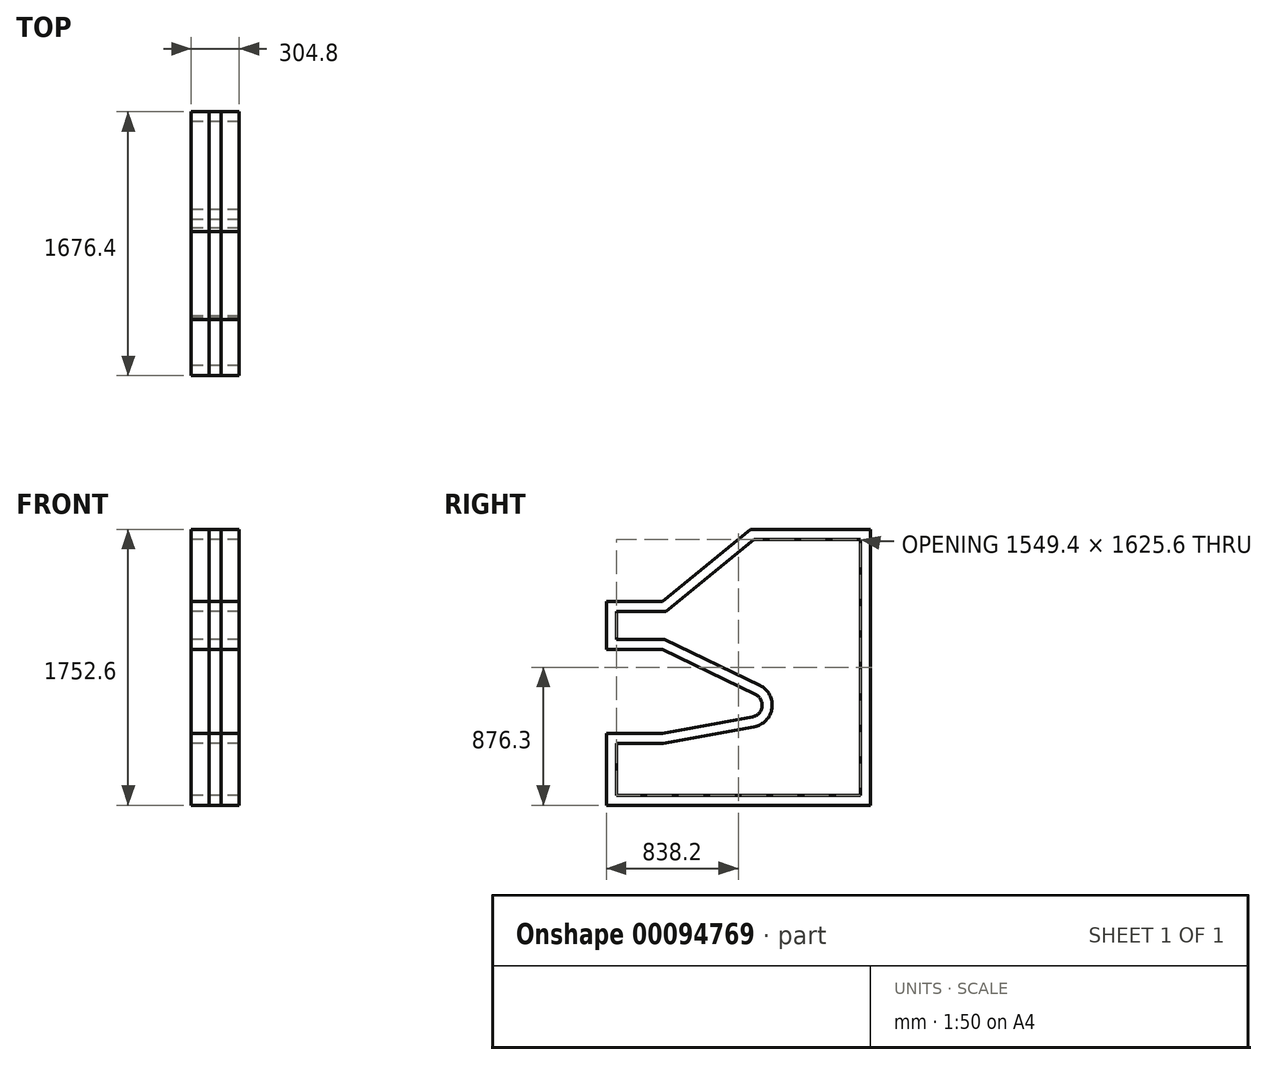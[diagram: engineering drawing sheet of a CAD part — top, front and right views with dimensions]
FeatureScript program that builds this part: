
annotation { "Feature Type Name" : "Feature", "Feature Type Description" : "" }
export const myFeature = defineFeature(function(context is Context, id is Id, definition is map)
    precondition{}
    {
        {
            var Q0;
            Q0=qCreatedBy(makeId("Right.planeOp"),FACE);
            var sketch = newSketch(context, id + "F0", { "sketchPlane" : qUnion([Q0])});
            skLineSegment(sketch, "E0", {"start": v(-914.4, 0) * mm, "end": v(762, 0) * mm, "construction": true});
            skLineSegment(sketch, "E1.0", {"start": v(-914.4, 457.2) * mm, "end": v(0, 457.2) * mm, "construction": true});
            skLineSegment(sketch, "E2.0", {"start": v(-1354.22, 635) * mm, "end": v(1358.95, 635) * mm, "construction": true});
            skLineSegment(sketch, "E3.0", {"start": v(-914.4, 990.6) * mm, "end": v(0, 990.6) * mm, "construction": true});
            skLineSegment(sketch, "E4.0", {"start": v(-914.4, 1295.4) * mm, "end": v(0, 1295.4) * mm, "construction": true});
            skLineSegment(sketch, "E5", {"start": v(-914.4, 1295.4) * mm, "end": v(-914.4, 0) * mm, "construction": true});
            skLineSegment(sketch, "E6.0", {"start": v(-558.8, 1295.4) * mm, "end": v(-558.8, 0) * mm, "construction": true});
            skLineSegment(sketch, "E7.0", {"start": v(-1354.22, 1752.6) * mm, "end": v(1358.95, 1752.6) * mm, "construction": true});
            skLineSegment(sketch, "E8", {"start": v(0, -258.78) * mm, "end": v(0, 1895.33) * mm, "construction": true});
            skLineSegment(sketch, "E9.0", {"start": v(762, -258.78) * mm, "end": v(762, 1895.33) * mm, "construction": true});
            skArc(sketch, "E10", {"start": v(13.47, 560) * mm, "mid": v(75.49, 624.6) * mm, "end": v(33.24, 703.57) * mm});
            skLineSegment(sketch, "E11", {"start": v(-558.8, 990.6) * mm, "end": v(33.24, 703.57) * mm});
            skLineSegment(sketch, "E12", {"start": v(-558.8, 457.2) * mm, "end": v(13.47, 560) * mm});
            skLineSegment(sketch, "E13", {"start": v(-558.8, 990.6) * mm, "end": v(-914.4, 990.6) * mm});
            skLineSegment(sketch, "E14", {"start": v(-914.4, 990.6) * mm, "end": v(-914.4, 1295.4) * mm});
            skLineSegment(sketch, "E15", {"start": v(-914.4, 1295.4) * mm, "end": v(-558.8, 1295.4) * mm});
            skLineSegment(sketch, "E16", {"start": v(-558.8, 1295.4) * mm, "end": v(0, 1752.6) * mm});
            skLineSegment(sketch, "E17", {"start": v(0, 1752.6) * mm, "end": v(762, 1752.6) * mm});
            skLineSegment(sketch, "E18", {"start": v(762, 1752.6) * mm, "end": v(762, 0) * mm});
            skLineSegment(sketch, "E19", {"start": v(-914.4, 0) * mm, "end": v(762, 0) * mm});
            skLineSegment(sketch, "E20", {"start": v(-914.4, 0) * mm, "end": v(-914.4, 457.2) * mm});
            skLineSegment(sketch, "E21", {"start": v(-914.4, 457.2) * mm, "end": v(-558.8, 457.2) * mm});
            skPoint(sketch, "E22.orphan", {"position": v(0, 557.58) * mm});
            skSolve(sketch);
        }
        {
            var Q0;
            Q0 = qSketchRegion(id + "F0", true);
            extrude(context, id + "F1", {"entities" : qUnion([Q0]), "endBound" : BoundingType.SYMMETRIC, "depth" : 76.2 * mm});
        }
        {
            var Q0;
            Q0=qCreatedBy(makeId("Right.planeOp"),FACE);
            var sketch = newSketch(context, id + "F2", { "sketchPlane" : qUnion([Q0])});
            skArc(sketch, "E23.0.0", {"start": v(33.24, 703.57) * mm, "mid": v(75.49, 624.6) * mm, "end": v(13.47, 560) * mm});
            skLineSegment(sketch, "E23.0.1", {"start": v(13.47, 560) * mm, "end": v(-558.8, 457.2) * mm});
            skLineSegment(sketch, "E23.0.2", {"start": v(-558.8, 457.2) * mm, "end": v(-914.4, 457.2) * mm});
            skLineSegment(sketch, "E23.0.3", {"start": v(-914.4, 457.2) * mm, "end": v(-914.4, 0) * mm});
            skLineSegment(sketch, "E23.0.4", {"start": v(-914.4, 0) * mm, "end": v(762, 0) * mm});
            skLineSegment(sketch, "E23.0.5", {"start": v(762, 0) * mm, "end": v(762, 1752.6) * mm});
            skLineSegment(sketch, "E23.0.6", {"start": v(762, 1752.6) * mm, "end": v(0, 1752.6) * mm});
            skLineSegment(sketch, "E23.0.7", {"start": v(0, 1752.6) * mm, "end": v(-558.8, 1295.4) * mm});
            skLineSegment(sketch, "E23.0.8", {"start": v(-558.8, 1295.4) * mm, "end": v(-914.4, 1295.4) * mm});
            skLineSegment(sketch, "E23.0.9", {"start": v(-914.4, 1295.4) * mm, "end": v(-914.4, 990.6) * mm});
            skLineSegment(sketch, "E23.0.10", {"start": v(-914.4, 990.6) * mm, "end": v(-558.8, 990.6) * mm});
            skLineSegment(sketch, "E23.0.11", {"start": v(-558.8, 990.6) * mm, "end": v(33.24, 703.57) * mm});
            skLineSegment(sketch, "E24.0", {"start": v(698.5, 63.5) * mm, "end": v(698.5, 1689.1) * mm});
            skLineSegment(sketch, "E24.1", {"start": v(-850.9, 1054.1) * mm, "end": v(-544.22, 1054.1) * mm});
            skLineSegment(sketch, "E24.2", {"start": v(-850.9, 1231.9) * mm, "end": v(-850.9, 1054.1) * mm});
            skLineSegment(sketch, "E24.3", {"start": v(-536.13, 1231.9) * mm, "end": v(-850.9, 1231.9) * mm});
            skLineSegment(sketch, "E24.4", {"start": v(22.67, 1689.1) * mm, "end": v(-536.13, 1231.9) * mm});
            skLineSegment(sketch, "E24.5", {"start": v(-544.22, 1054.1) * mm, "end": v(60.94, 760.7) * mm});
            skLineSegment(sketch, "E24.6", {"start": v(698.5, 1689.1) * mm, "end": v(22.67, 1689.1) * mm});
            skArc(sketch, "E24.7", {"start": v(60.94, 760.7) * mm, "mid": v(138.4, 615.94) * mm, "end": v(24.7, 497.5) * mm});
            skLineSegment(sketch, "E24.8", {"start": v(24.7, 497.5) * mm, "end": v(-553.14, 393.7) * mm});
            skLineSegment(sketch, "E24.9", {"start": v(-553.14, 393.7) * mm, "end": v(-850.9, 393.7) * mm});
            skLineSegment(sketch, "E24.10", {"start": v(-850.9, 393.7) * mm, "end": v(-850.9, 63.5) * mm});
            skLineSegment(sketch, "E24.11", {"start": v(-850.9, 63.5) * mm, "end": v(698.5, 63.5) * mm});
            skSolve(sketch);
        }
        {
            var Q0;
            Q0 = qSketchRegion(id + "F2", true);
            extrude(context, id + "F3", {"entities" : qUnion([Q0]), "endBound" : BoundingType.SYMMETRIC, "depth" : 304.8 * mm});
        }
    });
